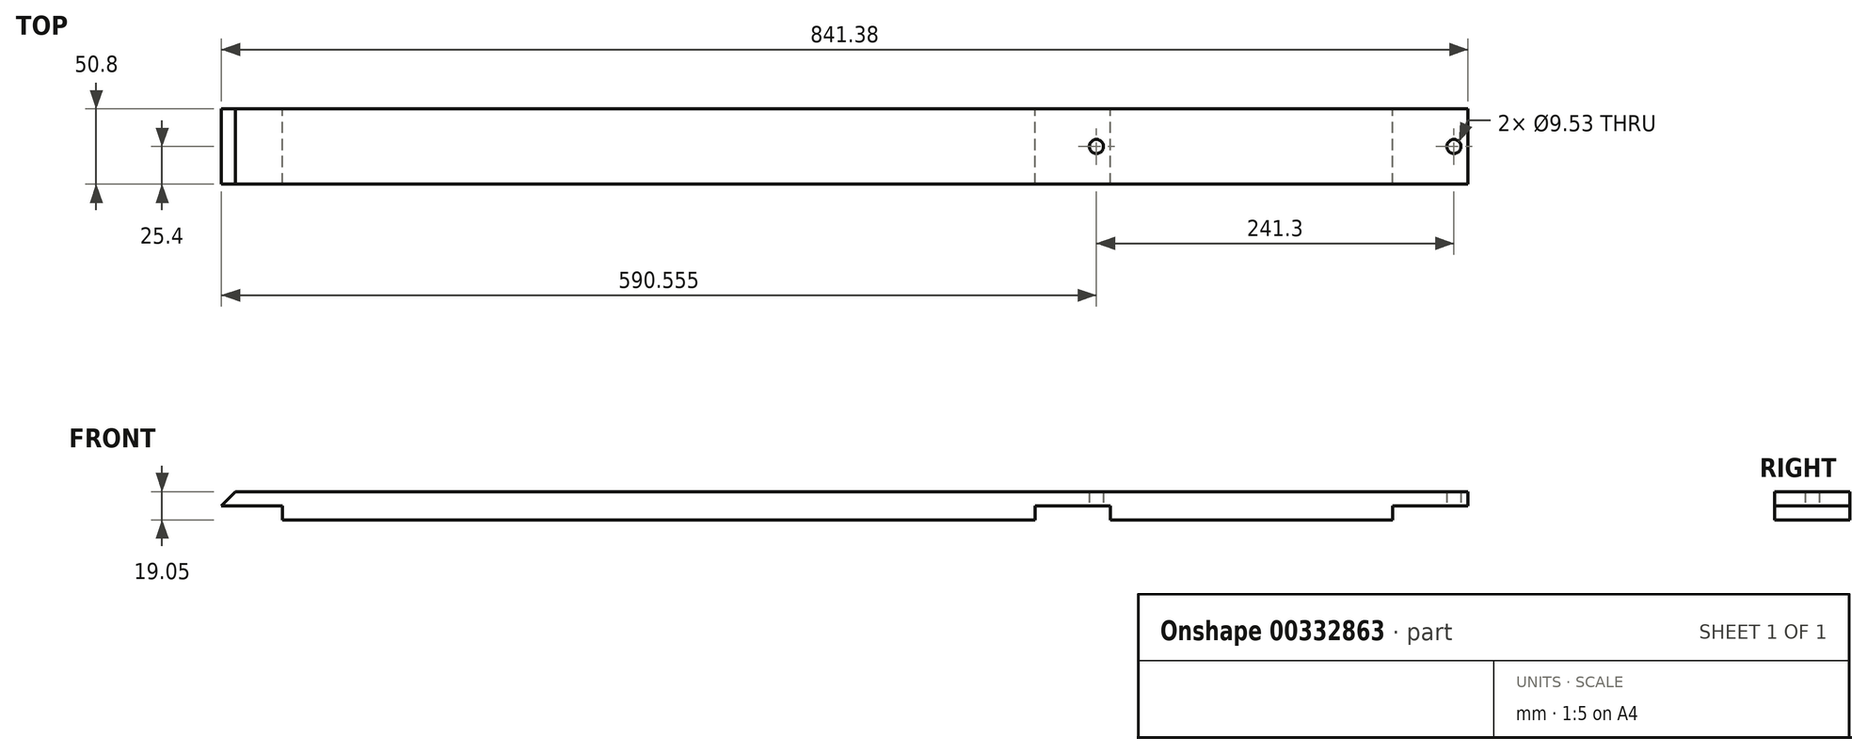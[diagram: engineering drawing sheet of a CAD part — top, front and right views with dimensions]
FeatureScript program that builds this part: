
annotation { "Feature Type Name" : "Feature", "Feature Type Description" : "" }
export const myFeature = defineFeature(function(context is Context, id is Id, definition is map)
    precondition{}
    {
        {
            var Q0;
            Q0=qCreatedBy(makeId("Front.planeOp"),FACE);
            var sketch = newSketch(context, id + "F0", { "sketchPlane" : qUnion([Q0])});
            skLineSegment(sketch, "E0.bottom", {"start": v(50.8, 0) * mm, "end": v(558.8, 0) * mm});
            skLineSegment(sketch, "E1", {"start": v(850.9, 19.05) * mm, "end": v(19.05, 19.05) * mm});
            skLineSegment(sketch, "E2.top", {"start": v(800.1, 9.52) * mm, "end": v(850.9, 9.52) * mm});
            skLineSegment(sketch, "E2.left", {"start": v(800.1, 0) * mm, "end": v(800.1, 9.52) * mm});
            skLineSegment(sketch, "E3", {"start": v(9.52, 9.52) * mm, "end": v(19.05, 19.05) * mm});
            skLineSegment(sketch, "E4", {"start": v(850.9, 9.52) * mm, "end": v(850.9, 19.05) * mm});
            skPoint(sketch, "E2.right.start.orphan", {"position": v(850.9, 0) * mm});
            skLineSegment(sketch, "E5.top", {"start": v(558.8, 9.52) * mm, "end": v(609.6, 9.52) * mm});
            skLineSegment(sketch, "E5.left", {"start": v(558.8, 0) * mm, "end": v(558.8, 9.52) * mm});
            skLineSegment(sketch, "E5.right", {"start": v(609.6, 0) * mm, "end": v(609.6, 9.52) * mm});
            skLineSegment(sketch, "E6.trimOffspring", {"start": v(609.6, 0) * mm, "end": v(800.1, 0) * mm});
            skLineSegment(sketch, "E7.top", {"start": v(9.52, 9.52) * mm, "end": v(50.8, 9.52) * mm});
            skLineSegment(sketch, "E7.right", {"start": v(50.8, 0) * mm, "end": v(50.8, 9.52) * mm});
            skPoint(sketch, "E8.end.orphan", {"position": v(0, 0) * mm});
            skSolve(sketch);
        }
        {
            var Q0;
            Q0=qSketchRegion(id+"F0",true);
            extrude(context, id + "F1", {"entities" : qUnion([Q0]), "depth" : 50.8 * mm});
        }
        {
            var Q0;
            Q0=qCreatedBy(makeId("Top.planeOp"),FACE);
            var sketch = newSketch(context, id + "F2", { "sketchPlane" : qUnion([Q0])});
            skCircle(sketch, "E9", {"center": v(841.38, -25.4) * mm, "radius": 4.76 * mm});
            skCircle(sketch, "E10", {"center": v(600.08, -25.4) * mm, "radius": 4.76 * mm});
            skSolve(sketch);
        }
        {
            var Q0;
            Q0 = qSketchRegion(id + "F2", true);
            extrude(context, id + "F3", {"entities" : qUnion([Q0]), "operationType" : NewBodyOperationType.REMOVE, "depth" : 25.4 * mm});
        }
    });
